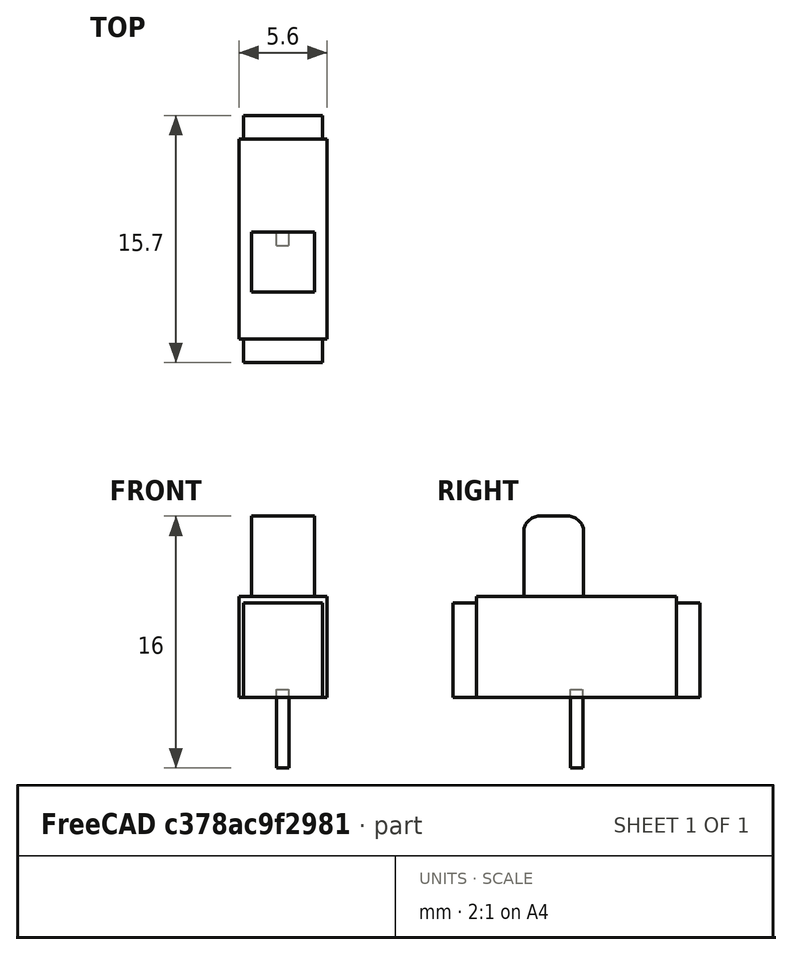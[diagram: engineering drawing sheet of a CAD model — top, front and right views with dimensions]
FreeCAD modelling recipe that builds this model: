
FCSTD DOCUMENT  (FreeCAD 0.21R33668 +26 (Git))
Label: Switch
License: All rights reserved
LicenseURL: http://en.wikipedia.org/wiki/All_rights_reserved
objects: Part::Box×5, Part::Fillet×2
note: 7 computed .brp shape members not serialized (recipe doc carries the construction recipe); baked Part::Feature solids carry a one-line shape summary decoded from their .brp

FEATURE [Part::Box] Box  label="Cube"
  AttacherType = Attacher::AttachEngine3D
  Height = 6.4
  Length = 5.6
  Width = 12.7
  expr: Height = 13.1 - 6.7
FEATURE [Part::Box] Box001  label="Cube001"
  AttacherType = Attacher::AttachEngine3D
  Height = 5.1
  Length = 4
  Placement = pos=(0.8,3,6.4) rot=(0,0,1;0rad)
  Width = 3.8
FEATURE [Part::Fillet] Fillet
  Base = -> Box001
  Edges = 1 edges r=1: [Edge10]
FEATURE [Part::Fillet] Fillet001
  Base = -> Fillet
  Edges = 1 edges r=1: [Edge14]
FEATURE [Part::Box] Box002  label="Cube002"
  AttacherType = Attacher::AttachEngine3D
  Height = 5
  Length = 0.8
  Placement = pos=(2.4,5.95,-4.5) rot=(0,0,1;0rad)
  Width = 0.8
FEATURE [Part::Box] Box003  label="Cube003"
  AttacherType = Attacher::AttachEngine3D
  Height = 6
  Length = 5
  Placement = pos=(0.3,12.7,0) rot=(0,0,1;0rad)
  Width = 1.5
  expr: .Placement.Base.y = 12.7
FEATURE [Part::Box] Box004  label="Cube004"
  AttacherType = Attacher::AttachEngine3D
  Height = 6
  Length = 5
  Placement = pos=(0.3,-1.5,0) rot=(0,0,1;0rad)
  Width = 1.5
